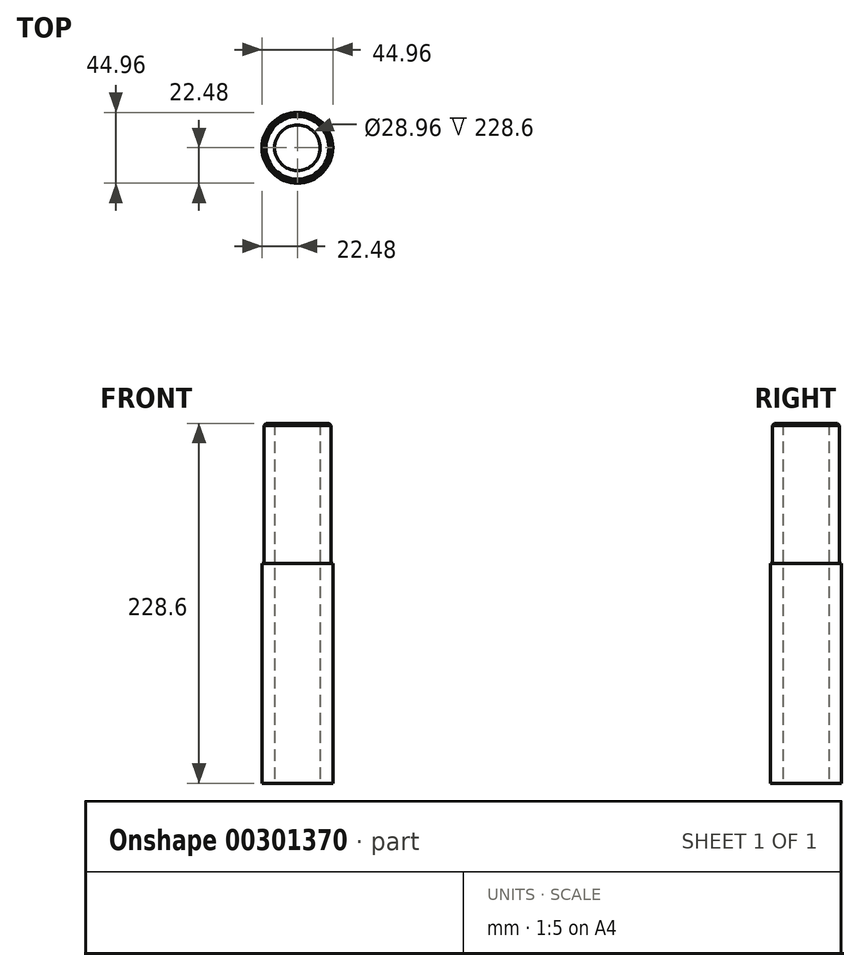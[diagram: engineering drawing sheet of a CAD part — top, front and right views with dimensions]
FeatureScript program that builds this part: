
annotation { "Feature Type Name" : "Feature", "Feature Type Description" : "" }
export const myFeature = defineFeature(function(context is Context, id is Id, definition is map)
    precondition{}
    {
        {
            var Q0;
            Q0=qCreatedBy(makeId("Top.planeOp"),FACE);
            var sketch = newSketch(context, id + "F0", { "sketchPlane" : qUnion([Q0])});
            skCircle(sketch, "E0", {"center": v(0, 0) * mm, "radius": 14.48 * mm});
            skCircle(sketch, "E1", {"center": v(0, 0) * mm, "radius": 22.48 * mm});
            skCircle(sketch, "E2", {"center": v(0, 0) * mm, "radius": 21.2 * mm});
            skSolve(sketch);
        }
        {
            var Q0;
            Q0=makeQuery(id+"F0.imprint","IMPRINT",FACE,{"disambiguationData":[TD([[makeQuery(id+"F0.imprint","IMPRINT",EDGE,{"derivedFrom":sQuery(id+"F0.wireOp",EDGE,"E1")}),1.0]])]});
            extrude(context, id + "F1", {"entities" : qUnion([Q0]), "flatOperationType" : FlatOperationType.REMOVE, "offsetDistance" : 25.4 * mm, "depth" : 139.7 * mm, "domain" : OperationDomain.MODEL});
        }
        {
            var Q0;
            Q0=makeQuery(id+"F0.imprint","IMPRINT",FACE,{"disambiguationData":[TD([[makeQuery(id+"F0.imprint","IMPRINT",EDGE,{"derivedFrom":sQuery(id+"F0.wireOp",EDGE,"E0")}),-1.0]])]});
            extrude(context, id + "F2", {"entities" : qUnion([Q0]), "operationType" : NewBodyOperationType.ADD, "flatOperationType" : FlatOperationType.REMOVE, "offsetDistance" : 25.4 * mm, "depth" : 228.6 * mm, "domain" : OperationDomain.MODEL});
        }
        {
            var Q0;
            Q0=makeQuery(id+"F2.opExtrude","CAP_EDGE",EDGE,{"disambiguationData":[OSD([sQuery(id+"F0.wireOp",EDGE,"E2")])],"isStart":false});
            chamfer(context, id + "F3", {"entities" : qUnion([Q0]), "width" : 1.27 * mm, "tangentPropagation" : true});
        }
    });
